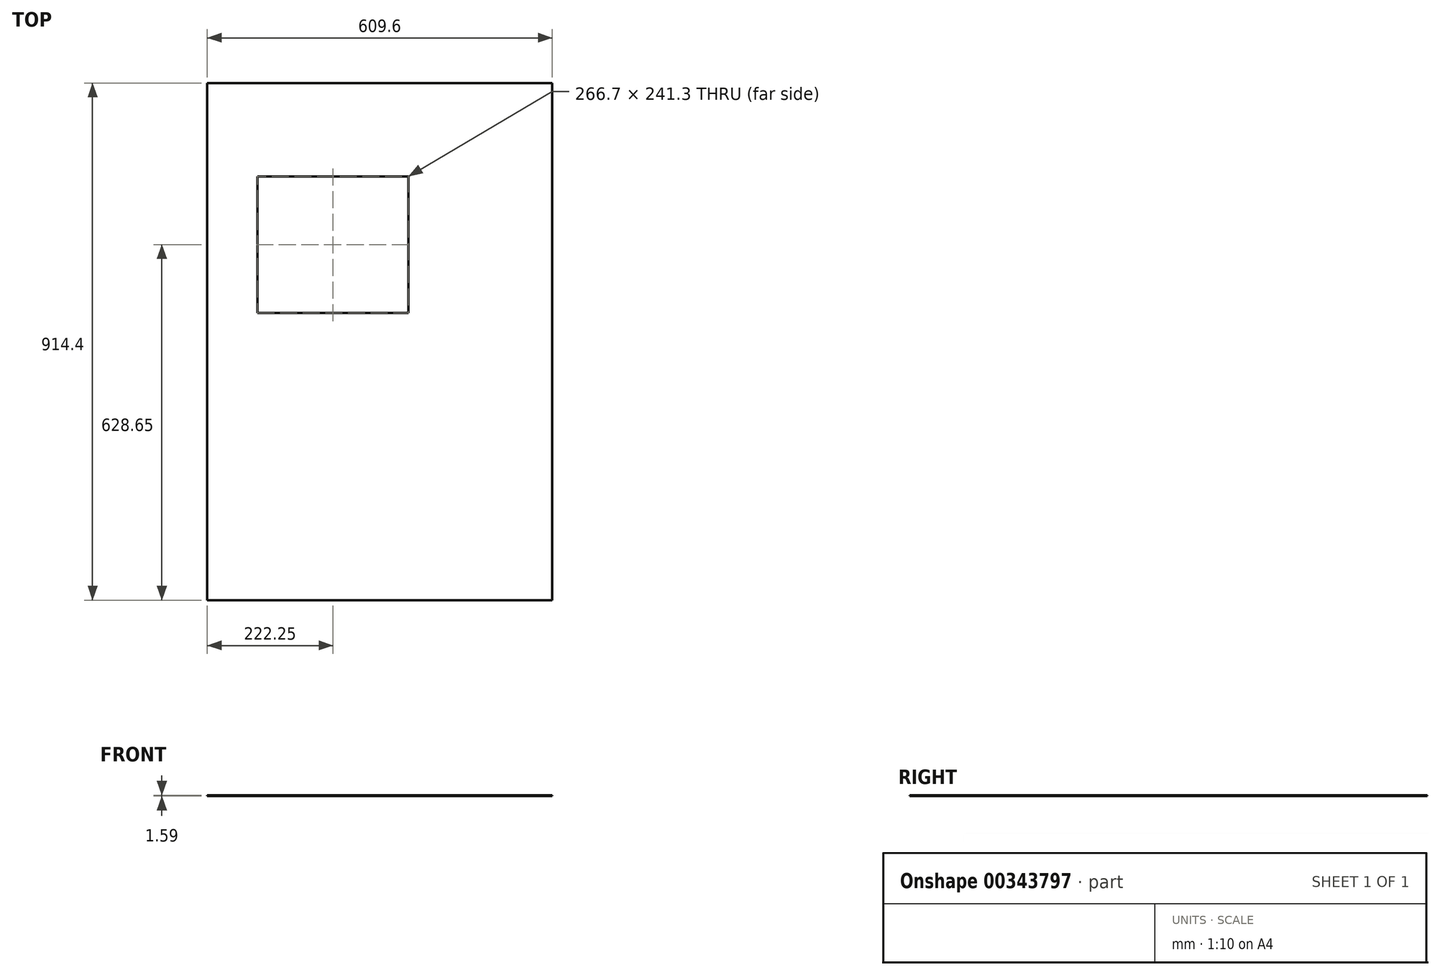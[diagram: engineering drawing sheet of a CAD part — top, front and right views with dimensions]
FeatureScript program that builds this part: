
annotation { "Feature Type Name" : "Feature", "Feature Type Description" : "" }
export const myFeature = defineFeature(function(context is Context, id is Id, definition is map)
    precondition{}
    {
        {
            var Q0;
            Q0=qCreatedBy(makeId("Top.planeOp"),FACE);
            var sketch = newSketch(context, id + "F0", { "sketchPlane" : qUnion([Q0])});
            skLineSegment(sketch, "E0.bottom", {"start": v(304.8, -457.2) * mm, "end": v(-304.8, -457.2) * mm});
            skLineSegment(sketch, "E0.top", {"start": v(304.8, 457.2) * mm, "end": v(-304.8, 457.2) * mm});
            skLineSegment(sketch, "E0.left", {"start": v(304.8, -457.2) * mm, "end": v(304.8, 457.2) * mm});
            skLineSegment(sketch, "E0.right", {"start": v(-304.8, -457.2) * mm, "end": v(-304.8, 457.2) * mm});
            skPoint(sketch, "E0.middle", {"position": v(0, 0) * mm});
            skSolve(sketch);
        }
        {
            var Q0;
            Q0=makeQuery(id+"F0.imprint","IMPRINT",FACE,{"disambiguationData":[TD([[makeQuery(id+"F0.imprint","IMPRINT",EDGE,{"derivedFrom":sQuery(id+"F0.wireOp",EDGE,"E0.bottom")}),-1.0]])]});
            extrude(context, id + "F1", {"entities" : qUnion([Q0]), "depth" : 1.59 * mm});
        }
        {
            var Q0;
            Q0=makeQuery(id+"F1.opExtrude","CAP_FACE",FACE,{"disambiguationData":[OSD([sQuery(id+"F0.wireOp",EDGE,"E0.bottom"),sQuery(id+"F0.wireOp",EDGE,"E0.top"),sQuery(id+"F0.wireOp",EDGE,"E0.left"),sQuery(id+"F0.wireOp",EDGE,"E0.right")])],"isStart":false});
            var sketch = newSketch(context, id + "F2", { "sketchPlane" : qUnion([Q0])});
            skLineSegment(sketch, "E1.bottom", {"start": v(-215.9, 292.1) * mm, "end": v(50.8, 292.1) * mm});
            skLineSegment(sketch, "E1.top", {"start": v(-215.9, 50.8) * mm, "end": v(50.8, 50.8) * mm});
            skLineSegment(sketch, "E1.left", {"start": v(-215.9, 292.1) * mm, "end": v(-215.9, 50.8) * mm});
            skLineSegment(sketch, "E1.right", {"start": v(50.8, 292.1) * mm, "end": v(50.8, 50.8) * mm});
            skSolve(sketch);
        }
        {
            var Q0;
            Q0=makeQuery(id+"F2.imprint","IMPRINT",FACE,{"disambiguationData":[TD([[makeQuery(id+"F2.imprint","IMPRINT",EDGE,{"derivedFrom":sQuery(id+"F2.wireOp",EDGE,"E1.bottom")}),-1.0]])]});
            extrude(context, id + "F3", {"entities" : qUnion([Q0]), "operationType" : NewBodyOperationType.REMOVE, "oppositeDirection" : true, "depth" : 25.4 * mm});
        }
    });
